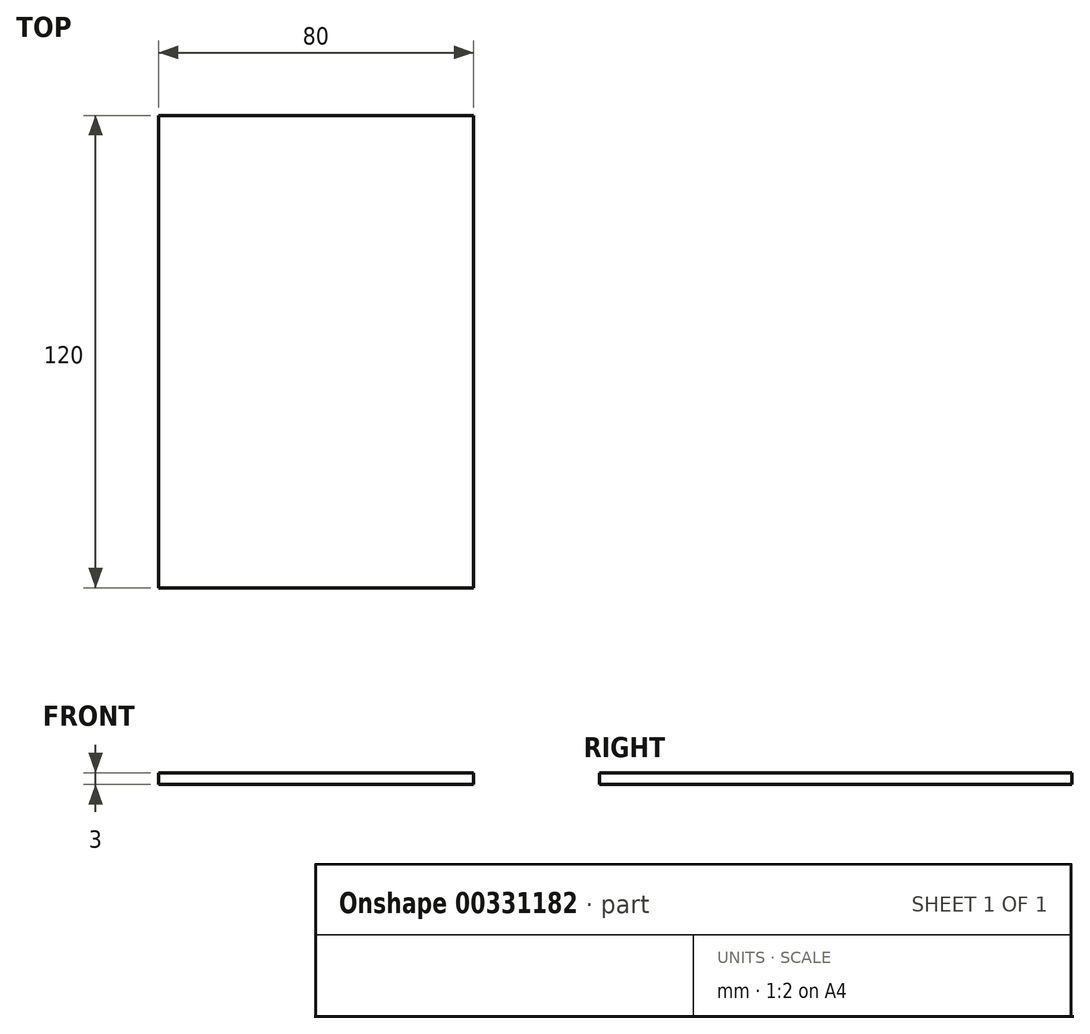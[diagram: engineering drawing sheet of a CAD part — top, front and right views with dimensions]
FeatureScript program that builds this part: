
annotation { "Feature Type Name" : "Feature", "Feature Type Description" : "" }
export const myFeature = defineFeature(function(context is Context, id is Id, definition is map)
    precondition{}
    {
        {
            var Q0;
            Q0=qCreatedBy(makeId("Top.planeOp"),FACE);
            var sketch = newSketch(context, id + "F0", { "sketchPlane" : qUnion([Q0])});
            skLineSegment(sketch, "E0.bottom", {"start": v(-40, 60) * mm, "end": v(40, 60) * mm});
            skLineSegment(sketch, "E0.top", {"start": v(-40, -60) * mm, "end": v(40, -60) * mm});
            skLineSegment(sketch, "E0.left", {"start": v(-40, 60) * mm, "end": v(-40, -60) * mm});
            skLineSegment(sketch, "E0.right", {"start": v(40, 60) * mm, "end": v(40, -60) * mm});
            skPoint(sketch, "E0.middle", {"position": v(0, 0) * mm});
            skSolve(sketch);
        }
        {
            var Q0;
            Q0 = qSketchRegion(id + "F0", true);
            extrude(context, id + "F1", {"entities" : qUnion([Q0]), "depth" : 3 * mm});
        }
    });
